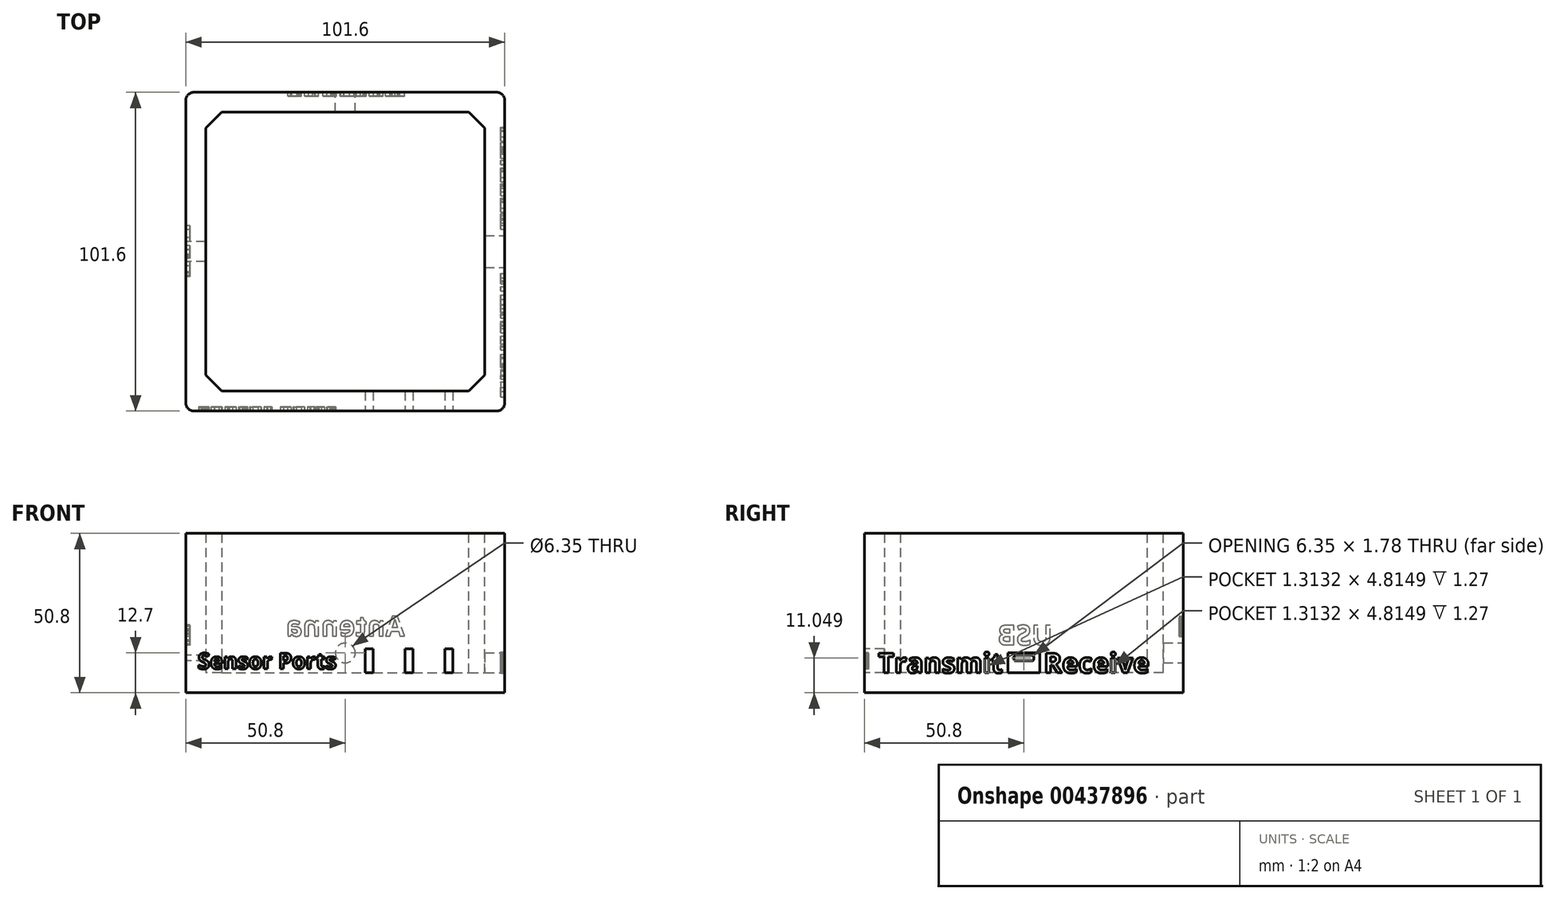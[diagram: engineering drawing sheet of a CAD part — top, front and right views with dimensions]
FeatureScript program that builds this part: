
annotation { "Feature Type Name" : "Feature", "Feature Type Description" : "" }
export const myFeature = defineFeature(function(context is Context, id is Id, definition is map)
    precondition{}
    {
        {
            var Q0;
            Q0=qCreatedBy(makeId("Top.planeOp"),FACE);
            var sketch = newSketch(context, id + "F0", { "sketchPlane" : qUnion([Q0])});
            skLineSegment(sketch, "E0.bottom", {"start": v(-50.8, 50.8) * mm, "end": v(50.8, 50.8) * mm});
            skLineSegment(sketch, "E0.top", {"start": v(-50.8, -50.8) * mm, "end": v(50.8, -50.8) * mm});
            skLineSegment(sketch, "E0.left", {"start": v(-50.8, 50.8) * mm, "end": v(-50.8, -50.8) * mm});
            skLineSegment(sketch, "E0.right", {"start": v(50.8, 50.8) * mm, "end": v(50.8, -50.8) * mm});
            skPoint(sketch, "E1", {"position": v(0, 50.8) * mm});
            skPoint(sketch, "E2", {"position": v(-50.8, 0) * mm});
            skSolve(sketch);
        }
        {
            var Q0;
            Q0=makeQuery(id+"F0.imprint","IMPRINT",FACE,{"disambiguationData":[TD([[makeQuery(id+"F0.imprint","IMPRINT",EDGE,{"derivedFrom":sQuery(id+"F0.wireOp",EDGE,"E0.bottom")}),-1.0]])]});
            extrude(context, id + "F1", {"entities" : qUnion([Q0]), "depth" : 50.8 * mm});
        }
        {
            var Q0;
            Q0=makeQuery(id+"F1.opExtrude","CAP_FACE",FACE,{"disambiguationData":[OSD([sQuery(id+"F0.wireOp",EDGE,"E0.bottom"),sQuery(id+"F0.wireOp",EDGE,"E0.top"),sQuery(id+"F0.wireOp",EDGE,"E0.left"),sQuery(id+"F0.wireOp",EDGE,"E0.right")])],"isStart":false});
            shell(context, id + "F2", {"entities" : qUnion([Q0]), "thickness" : 6.35 * mm});
        }
        {
            var Q0;
            Q0=makeQuery(id+"F1.opExtrude","SWEPT_FACE",FACE,{"disambiguationData":[OSD([sQuery(id+"F0.wireOp",EDGE,"E0.right")])]});
            var sketch = newSketch(context, id + "F3", { "sketchPlane" : qUnion([Q0])});
            skText(sketch, "E3", { "text": "Transmit", "fontName": "OpenSans-Bold.ttf"});
            skText(sketch, "E4", { "text": "Receive", "fontName": "OpenSans-Bold.ttf"});
            const initialGuessF3  = {"E3": [-0.04644, 0.00635, 1, 0, 0.00635], "E4": [0.00635, 0.00635, 1, 0, 0.00635]};
            skSetInitialGuess(sketch, initialGuessF3);
            skSolve(sketch);
        }
        {
            var Q0;
            Q0 = qSketchRegion(id + "F3", true);
            extrude(context, id + "F4", {"entities" : qUnion([Q0]), "operationType" : NewBodyOperationType.REMOVE, "oppositeDirection" : true, "depth" : 1.27 * mm});
        }
        {
            var Q0;
            {var subQ0=sQuery(id+"F0.wireOp",EDGE,"E0.bottom");var subQ1=sQuery(id+"F0.wireOp",EDGE,"E0.right");Q0=makeQuery(id+"F4.boolean.opBoolean","SPLIT",FACE,{"disambiguationData":[TD([makeQuery(id+"F1.opExtrude","SWEPT_FACE",FACE,{"disambiguationData":[OSD([subQ0])]})])],"derivedFrom":makeQuery(id+"F1.opExtrude","SWEPT_FACE",FACE,{"disambiguationData":[OSD([subQ1])]})});}
            var sketch = newSketch(context, id + "F5", { "sketchPlane" : qUnion([Q0])});
            skLineSegment(sketch, "E5.bottom", {"start": v(-5.08, 12.7) * mm, "end": v(5.08, 12.7) * mm});
            skLineSegment(sketch, "E5.top", {"start": v(-5.08, 6.35) * mm, "end": v(5.08, 6.35) * mm});
            skLineSegment(sketch, "E5.left", {"start": v(-5.08, 12.7) * mm, "end": v(-5.08, 6.35) * mm});
            skLineSegment(sketch, "E5.right", {"start": v(5.08, 12.7) * mm, "end": v(5.08, 6.35) * mm});
            skPoint(sketch, "E6", {"position": v(0, 12.7) * mm});
            skSolve(sketch);
        }
        {
            var Q0;
            Q0=makeQuery(id+"F5.imprint","IMPRINT",FACE,{"disambiguationData":[TD([[makeQuery(id+"F5.imprint","IMPRINT",EDGE,{"derivedFrom":sQuery(id+"F5.wireOp",EDGE,"E5.bottom")}),-1.0]])]});
            extrude(context, id + "F6", {"entities" : qUnion([Q0]), "operationType" : NewBodyOperationType.REMOVE, "oppositeDirection" : true, "depth" : 12.7 * mm});
        }
        {
            var Q0;
            Q0=makeQuery(id+"F1.opExtrude","SWEPT_FACE",FACE,{"disambiguationData":[OSD([sQuery(id+"F0.wireOp",EDGE,"E0.bottom")])]});
            var sketch = newSketch(context, id + "F7", { "sketchPlane" : qUnion([Q0])});
            skText(sketch, "E7", { "text": "Antenna", "fontName": "OpenSans-Bold.ttf"});
            const initialGuessF7  = {"E7": [-0.01887, 0.0181, 1, 0, 0.00635]};
            skSetInitialGuess(sketch, initialGuessF7);
            skSolve(sketch);
        }
        {
            var Q0;
            Q0=makeQuery(id+"F7.imprint","IMPRINT",FACE,{"disambiguationData":[TD([[makeQuery(id+"F7.imprint","IMPRINT",EDGE,{"derivedFrom":sQuery(id+"F7.wireOp",EDGE,"E7.sketch_text.stroke-0")}),1.0]])]});
            var sketch = newSketch(context, id + "F8", { "sketchPlane" : qUnion([Q0])});
            skCircle(sketch, "E8", {"center": v(0, 12.7) * mm, "radius": 3.17 * mm});
            skSolve(sketch);
        }
        {
            var Q0;
            Q0=makeQuery(id+"F8.imprint","IMPRINT",FACE,{"disambiguationData":[TD([[makeQuery(id+"F8.imprint","IMPRINT",EDGE,{"derivedFrom":sQuery(id+"F8.wireOp",EDGE,"E8")}),1.0]])]});
            extrude(context, id + "F9", {"entities" : qUnion([Q0]), "operationType" : NewBodyOperationType.REMOVE, "oppositeDirection" : true, "depth" : 25.4 * mm});
        }
        {
            var Q0;
            Q0 = qSketchRegion(id + "F7", true);
            extrude(context, id + "F10", {"entities" : qUnion([Q0]), "operationType" : NewBodyOperationType.REMOVE, "oppositeDirection" : true, "depth" : 1.27 * mm});
        }
        {
            var Q0;
            Q0=makeQuery(id+"F1.opExtrude","SWEPT_FACE",FACE,{"disambiguationData":[OSD([sQuery(id+"F0.wireOp",EDGE,"E0.left")])]});
            var sketch = newSketch(context, id + "F11", { "sketchPlane" : qUnion([Q0])});
            skLineSegment(sketch, "E9.bottom", {"start": v(-2.54, 11.94) * mm, "end": v(2.54, 11.94) * mm});
            skLineSegment(sketch, "E9.top", {"start": v(-2.54, 10.16) * mm, "end": v(2.54, 10.16) * mm});
            skLineSegment(sketch, "E9.left", {"start": v(-3.18, 11.3) * mm, "end": v(-3.18, 10.8) * mm});
            skLineSegment(sketch, "E9.right", {"start": v(3.18, 11.3) * mm, "end": v(3.18, 10.8) * mm});
            skPoint(sketch, "E10", {"position": v(0, 11.94) * mm});
            skPoint(sketch, "E11.visualSharp", {"position": v(3.17, 11.94) * mm});
            skArc(sketch, "E11.filletArc", {"start": v(3.17, 11.3) * mm, "mid": v(2.99, 11.75) * mm, "end": v(2.54, 11.94) * mm});
            skPoint(sketch, "E12.visualSharp", {"position": v(3.17, 10.16) * mm});
            skArc(sketch, "E12.filletArc", {"start": v(2.54, 10.16) * mm, "mid": v(2.99, 10.35) * mm, "end": v(3.17, 10.8) * mm});
            skPoint(sketch, "E13.visualSharp", {"position": v(-3.18, 11.94) * mm});
            skArc(sketch, "E13.filletArc", {"start": v(-2.54, 11.94) * mm, "mid": v(-2.99, 11.75) * mm, "end": v(-3.18, 11.3) * mm});
            skPoint(sketch, "E14.visualSharp", {"position": v(-3.18, 10.16) * mm});
            skArc(sketch, "E14.filletArc", {"start": v(-3.18, 10.8) * mm, "mid": v(-2.99, 10.35) * mm, "end": v(-2.54, 10.16) * mm});
            skSolve(sketch);
        }
        {
            var Q0;
            Q0=makeQuery(id+"F11.imprint","IMPRINT",FACE,{"disambiguationData":[TD([[makeQuery(id+"F11.imprint","IMPRINT",EDGE,{"derivedFrom":sQuery(id+"F11.wireOp",EDGE,"E9.bottom")}),-1.0]])]});
            extrude(context, id + "F12", {"entities" : qUnion([Q0]), "operationType" : NewBodyOperationType.REMOVE, "oppositeDirection" : true, "depth" : 25.4 * mm});
        }
        {
            var Q0;
            Q0=makeQuery(id+"F1.opExtrude","SWEPT_FACE",FACE,{"disambiguationData":[OSD([sQuery(id+"F0.wireOp",EDGE,"E0.left")])]});
            var sketch = newSketch(context, id + "F13", { "sketchPlane" : qUnion([Q0])});
            skText(sketch, "E15", { "text": "USB", "fontName": "OpenSans-Bold.ttf"});
            const initialGuessF13  = {"E15": [-0.00908, 0.01524, 1, 0, 0.00635]};
            skSetInitialGuess(sketch, initialGuessF13);
            skSolve(sketch);
        }
        {
            var Q0;
            Q0 = qSketchRegion(id + "F13", true);
            extrude(context, id + "F14", {"entities" : qUnion([Q0]), "operationType" : NewBodyOperationType.REMOVE, "oppositeDirection" : true, "depth" : 1.27 * mm});
        }
        {
            var Q0;
            Q0=makeQuery(id+"F1.opExtrude","SWEPT_FACE",FACE,{"disambiguationData":[OSD([sQuery(id+"F0.wireOp",EDGE,"E0.top")])]});
            var sketch = newSketch(context, id + "F15", { "sketchPlane" : qUnion([Q0])});
            skLineSegment(sketch, "E16.bottom", {"start": v(6.35, 13.97) * mm, "end": v(8.9, 13.97) * mm});
            skLineSegment(sketch, "E16.top", {"start": v(6.35, 6.35) * mm, "end": v(8.9, 6.35) * mm});
            skLineSegment(sketch, "E16.left", {"start": v(6.35, 13.97) * mm, "end": v(6.35, 6.35) * mm});
            skLineSegment(sketch, "E16.right", {"start": v(8.9, 13.97) * mm, "end": v(8.9, 6.35) * mm});
            skLineSegment(sketch, "E17.1.0.0", {"start": v(19.05, 13.97) * mm, "end": v(21.6, 13.97) * mm});
            skLineSegment(sketch, "E17.1.0.1", {"start": v(21.6, 13.97) * mm, "end": v(21.6, 6.35) * mm});
            skLineSegment(sketch, "E17.1.0.2", {"start": v(19.05, 6.35) * mm, "end": v(21.6, 6.35) * mm});
            skLineSegment(sketch, "E17.1.0.3", {"start": v(19.05, 13.97) * mm, "end": v(19.05, 6.35) * mm});
            skLineSegment(sketch, "E17.2.0.0", {"start": v(31.75, 13.97) * mm, "end": v(34.3, 13.97) * mm});
            skLineSegment(sketch, "E17.2.0.1", {"start": v(34.3, 13.97) * mm, "end": v(34.3, 6.35) * mm});
            skLineSegment(sketch, "E17.2.0.2", {"start": v(31.75, 6.35) * mm, "end": v(34.3, 6.35) * mm});
            skLineSegment(sketch, "E17.2.0.3", {"start": v(31.75, 13.97) * mm, "end": v(31.75, 6.35) * mm});
            skLineSegment(sketch, "E17.direction1", {"start": v(6.35, 13.97) * mm, "end": v(19.05, 13.97) * mm, "construction": true});
            skSolve(sketch);
        }
        {
            var Q0;
            Q0=makeQuery(id+"F15.imprint","IMPRINT",FACE,{"disambiguationData":[TD([[makeQuery(id+"F15.imprint","IMPRINT",EDGE,{"derivedFrom":sQuery(id+"F15.wireOp",EDGE,"E16.bottom")}),1.0]])]});
            var sketch = newSketch(context, id + "F16", { "sketchPlane" : qUnion([Q0])});
            skText(sketch, "E18", { "text": "Sensor Ports", "fontName": "OpenSans-Bold.ttf"});
            const initialGuessF16  = {"E18": [-0.047, 0.00762, 1, 0, 0.00508]};
            skSetInitialGuess(sketch, initialGuessF16);
            skSolve(sketch);
        }
        {
            var Q0;
            Q0 = qSketchRegion(id + "F16", true);
            extrude(context, id + "F17", {"entities" : qUnion([Q0]), "operationType" : NewBodyOperationType.REMOVE, "oppositeDirection" : true, "depth" : 1.27 * mm});
        }
        {
            var Q0;
            Q0 = qSketchRegion(id + "F15", true);
            extrude(context, id + "F18", {"entities" : qUnion([Q0]), "operationType" : NewBodyOperationType.REMOVE, "oppositeDirection" : true, "depth" : 25.4 * mm});
        }
        {
            var Q0;
            Q0=makeQuery(id+"F1.opExtrude","SWEPT_EDGE",EDGE,{"disambiguationData":[OSD([sQuery(id+"F0.wireOp",EDGE,"E0.top"),sQuery(id+"F0.wireOp",EDGE,"E0.left")])]});
            var Q1;
            Q1=makeQuery(id+"F1.opExtrude","SWEPT_EDGE",EDGE,{"disambiguationData":[OSD([sQuery(id+"F0.wireOp",EDGE,"E0.top"),sQuery(id+"F0.wireOp",EDGE,"E0.right")])]});
            var Q2;
            Q2=makeQuery(id+"F1.opExtrude","SWEPT_EDGE",EDGE,{"disambiguationData":[OSD([sQuery(id+"F0.wireOp",EDGE,"E0.bottom"),sQuery(id+"F0.wireOp",EDGE,"E0.right")])]});
            var Q3;
            Q3=makeQuery(id+"F1.opExtrude","SWEPT_EDGE",EDGE,{"disambiguationData":[OSD([sQuery(id+"F0.wireOp",EDGE,"E0.bottom"),sQuery(id+"F0.wireOp",EDGE,"E0.left")])]});
            fillet(context, id + "F19", {"entities" : qUnion([Q0, Q1, Q2, Q3]), "radius" : 2.54 * mm, "tangentPropagation" : true, "allowEdgeOverflow" : false});
        }
        {
            var Q0;
            Q0=makeQuery(id+"F2.opShell","OFFSET_EDGE",EDGE,{"disambiguationData":[OSD([sQuery(id+"F0.wireOp",EDGE,"E0.bottom"),sQuery(id+"F0.wireOp",EDGE,"E0.left")])]});
            var Q1;
            Q1=makeQuery(id+"F2.opShell","OFFSET_EDGE",EDGE,{"disambiguationData":[OSD([sQuery(id+"F0.wireOp",EDGE,"E0.bottom"),sQuery(id+"F0.wireOp",EDGE,"E0.right")])]});
            var Q2;
            Q2=makeQuery(id+"F2.opShell","OFFSET_EDGE",EDGE,{"disambiguationData":[OSD([sQuery(id+"F0.wireOp",EDGE,"E0.top"),sQuery(id+"F0.wireOp",EDGE,"E0.right")])]});
            var Q3;
            Q3=makeQuery(id+"F2.opShell","OFFSET_EDGE",EDGE,{"disambiguationData":[OSD([sQuery(id+"F0.wireOp",EDGE,"E0.top"),sQuery(id+"F0.wireOp",EDGE,"E0.left")])]});
            chamfer(context, id + "F20", {"entities" : qUnion([Q0, Q1, Q2, Q3]), "width" : 5.08 * mm, "tangentPropagation" : true});
        }
    });
